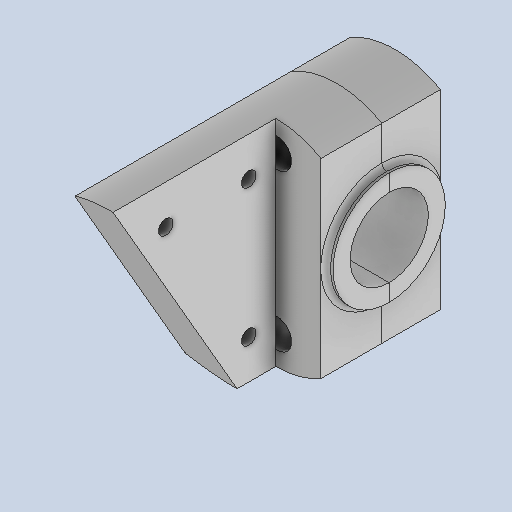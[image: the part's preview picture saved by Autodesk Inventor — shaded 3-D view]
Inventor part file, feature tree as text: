
AUTODESK INVENTOR PART (.ipt)
format: ipt  version: 2025.1 (Build 291241000, 241)  size: 208,384 bytes
history: native  units: mm
features: sketch x10, plane x4, other x3
ambient origin geometry x8: Origin, YZ Plane, XZ Plane, XY Plane, X Axis, Y Axis, Z Axis, Center Point
bodies: Volumenkörper1 (feature_tree)
feature tree (17):
  other  "1042.ipt"
  other  "Volumenkörper1::1042.ipt"
  other  "TaggingFeature1"
  sketch  "Skizze1"  dims[d0=10.0mm]
  sketch  "Skizze2"
  sketch  "Skizze8"
  sketch  "Skizze9"
  sketch  "Skizze10"
  sketch  "Skizze11"
  sketch  "Skizze17"
  sketch  "Skizze22"
  sketch  "Skizze25"
  sketch  "Skizze26"
  plane  "Arbeitsebene1"
  plane  "Arbeitsebene2"
  plane  "Arbeitsebene3"
  plane  "Arbeitsebene8"
